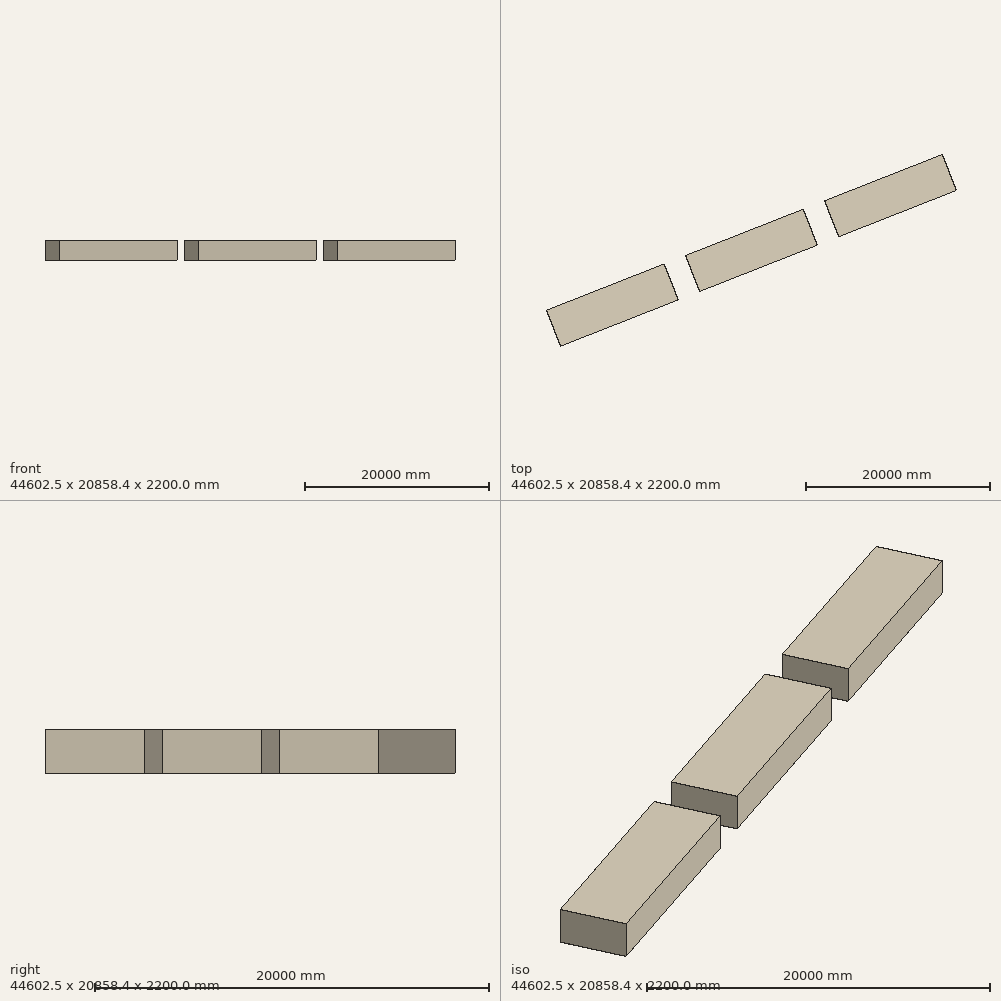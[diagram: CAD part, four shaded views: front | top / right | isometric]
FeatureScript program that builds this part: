
annotation { "Feature Type Name" : "Feature", "Feature Type Description" : "" }
export const myFeature = defineFeature(function(context is Context, id is Id, definition is map)
    precondition{}
    {
        {
            var Q0;
            Q0=qCreatedBy(makeId("Top.planeOp"),FACE);
            var sketch = newSketch(context, id + "F0", { "sketchPlane" : qUnion([Q0])});
            skLineSegment(sketch, "E0", {"start": v(29476.65, 3676.16) * mm, "end": v(-13587.58, -13274.08) * mm});
            skLineSegment(sketch, "E1", {"start": v(29476.65, 3676.16) * mm, "end": v(27938.38, 7584.33) * mm});
            skLineSegment(sketch, "E2", {"start": v(27938.38, 7584.33) * mm, "end": v(15134.5, 2544.67) * mm});
            skLineSegment(sketch, "E3", {"start": v(15134.5, 2544.67) * mm, "end": v(16672.76, -1363.5) * mm});
            skLineSegment(sketch, "E4", {"start": v(16672.76, -1363.5) * mm, "end": v(14346.48, -2279.13) * mm});
            skLineSegment(sketch, "E5", {"start": v(14346.48, -2279.13) * mm, "end": v(12808.2, 1629.03) * mm});
            skLineSegment(sketch, "E6", {"start": v(12808.2, 1629.03) * mm, "end": v(4.32, -3410.63) * mm});
            skLineSegment(sketch, "E7", {"start": v(4.32, -3410.63) * mm, "end": v(1542.6, -7318.79) * mm});
            skLineSegment(sketch, "E8", {"start": v(1542.6, -7318.79) * mm, "end": v(-783.7, -8234.43) * mm});
            skLineSegment(sketch, "E9", {"start": v(-783.7, -8234.43) * mm, "end": v(-2321.96, -4326.26) * mm});
            skLineSegment(sketch, "E10", {"start": v(-2321.96, -4326.26) * mm, "end": v(-15125.85, -9365.92) * mm});
            skLineSegment(sketch, "E11", {"start": v(-15125.85, -9365.92) * mm, "end": v(-13587.58, -13274.08) * mm});
            skLineSegment(sketch, "E12.bottom", {"start": v(-2886.84, 13395.2) * mm, "end": v(58207.41, 13395.2) * mm});
            skLineSegment(sketch, "E12.top", {"start": v(-2886.84, 12795.2) * mm, "end": v(58207.41, 12795.2) * mm});
            skLineSegment(sketch, "E12.left", {"start": v(-2886.84, 13395.2) * mm, "end": v(-2886.84, 12795.2) * mm});
            skLineSegment(sketch, "E12.right", {"start": v(58207.41, 13395.2) * mm, "end": v(58207.41, 12795.2) * mm});
            skLineSegment(sketch, "E13", {"start": v(27938.38, 7584.33) * mm, "end": v(25887.35, 12795.2) * mm});
            skLineSegment(sketch, "E14", {"start": v(12808.2, 1629.03) * mm, "end": v(8413.16, 12795.2) * mm});
            skLineSegment(sketch, "E15", {"start": v(4.32, -3410.63) * mm, "end": v(8413.16, 12795.2) * mm});
            skLineSegment(sketch, "E16", {"start": v(8413.16, 12795.2) * mm, "end": v(27938.38, 7584.33) * mm});
            skLineSegment(sketch, "E17", {"start": v(-2886.84, 12795.2) * mm, "end": v(19559.98, 12795.2) * mm});
            skLineSegment(sketch, "E18", {"start": v(19559.98, 12795.2) * mm, "end": v(22120.3, 6274.43) * mm});
            skLineSegment(sketch, "E19", {"start": v(22120.3, 6274.43) * mm, "end": v(12067.45, 2327.27) * mm});
            skLineSegment(sketch, "E20", {"start": v(12067.45, 2327.27) * mm, "end": v(10313.16, 6795.2) * mm});
            skLineSegment(sketch, "E21", {"start": v(10313.16, 6795.2) * mm, "end": v(-2886.84, 6795.2) * mm});
            skLineSegment(sketch, "E22", {"start": v(-2886.84, 6795.2) * mm, "end": v(-2886.84, 12795.2) * mm});
            skLineSegment(sketch, "E23", {"start": v(10313.16, 6795.2) * mm, "end": v(10313.16, 12795.2) * mm});
            skLineSegment(sketch, "E24", {"start": v(10313.16, 6795.2) * mm, "end": v(14403.24, 12795.2) * mm});
            skLineSegment(sketch, "E25", {"start": v(10313.16, 6795.2) * mm, "end": v(10313.16, 2327.27) * mm});
            skLineSegment(sketch, "E26", {"start": v(10313.16, 2327.27) * mm, "end": v(12067.45, 2327.27) * mm});
            skLineSegment(sketch, "E27", {"start": v(19559.98, 12795.2) * mm, "end": v(79869.68, 12795.2) * mm});
            skLineSegment(sketch, "E28", {"start": v(-2886.84, 11595.2) * mm, "end": v(13585.22, 11595.2) * mm});
            skPoint(sketch, "E29.endSnap0", {"position": v(17093.88, 4300.85) * mm});
            skLineSegment(sketch, "E30", {"start": v(-2886.84, 9195.2) * mm, "end": v(11949.19, 9195.2) * mm});
            skLineSegment(sketch, "E31", {"start": v(-2886.84, 7995.2) * mm, "end": v(11131.17, 7995.2) * mm});
            skLineSegment(sketch, "E32", {"start": v(-2886.84, 10395.2) * mm, "end": v(12767.2, 10395.2) * mm});
            skLineSegment(sketch, "E33", {"start": v(11628.88, 3444.26) * mm, "end": v(21681.73, 7391.42) * mm});
            skLineSegment(sketch, "E34", {"start": v(11190.3, 4561.24) * mm, "end": v(21243.16, 8508.4) * mm});
            skLineSegment(sketch, "E35", {"start": v(10751.73, 5678.22) * mm, "end": v(20804.59, 9625.39) * mm});
            skLineSegment(sketch, "E36", {"start": v(10313.16, 6795.2) * mm, "end": v(20366.01, 10742.37) * mm});
            skLineSegment(sketch, "E37", {"start": v(6713.16, 12795.2) * mm, "end": v(6713.16, 6795.2) * mm});
            skLineSegment(sketch, "E38", {"start": v(11131.17, 7995.2) * mm, "end": v(13184.43, 2765.85) * mm});
            skSolve(sketch);
        }
        {
            var Q0;
            {var subQ2=sQuery(id+"F0.wireOp",EDGE,"E9");Q0=makeQuery(id+"F0.imprint","IMPRINT",FACE,{"disambiguationData":[TD([[makeQuery(id+"F0.imprint","IMPRINT",EDGE,{"derivedFrom":subQ2}),1.0]])]});}
            var Q1;
            {var subQ0=sQuery(id+"F0.wireOp",EDGE,"E5");Q1=makeQuery(id+"F0.imprint","IMPRINT",FACE,{"disambiguationData":[TD([[makeQuery(id+"F0.imprint","IMPRINT",EDGE,{"derivedFrom":subQ0}),1.0]])]});}
            var Q2;
            {var subQ0=sQuery(id+"F0.wireOp",EDGE,"E1");Q2=makeQuery(id+"F0.imprint","IMPRINT",FACE,{"disambiguationData":[TD([[makeQuery(id+"F0.imprint","IMPRINT",EDGE,{"derivedFrom":subQ0}),1.0]])]});}
            extrude(context, id + "F1", {"entities" : qUnion([Q0, Q1, Q2]), "depth" : 2200 * mm, "offsetDistance" : 25 * mm});
        }
    });
